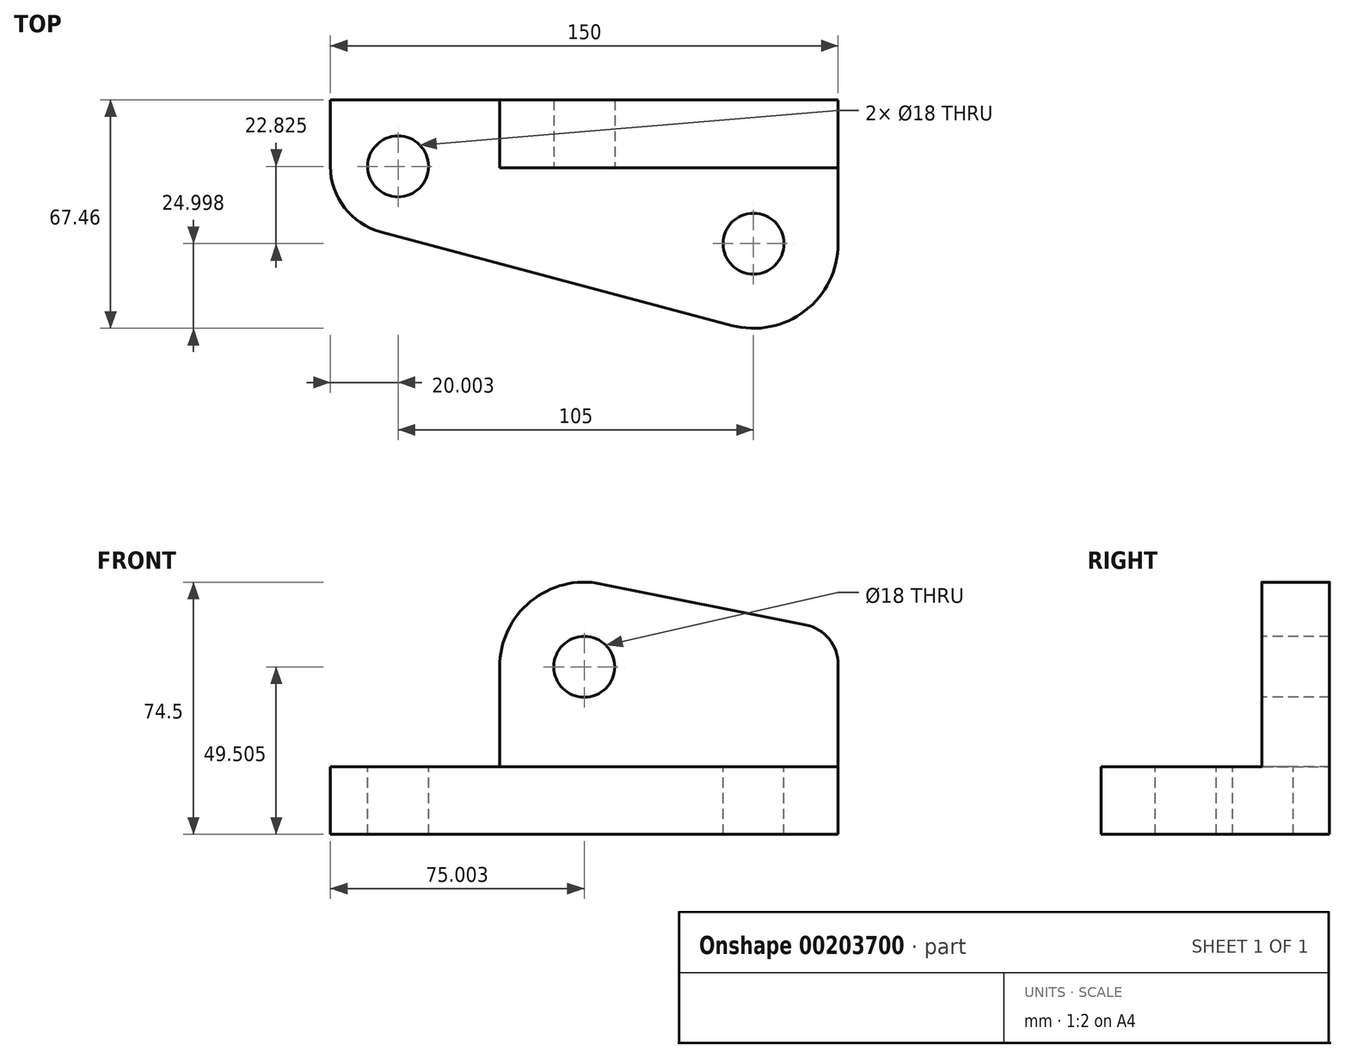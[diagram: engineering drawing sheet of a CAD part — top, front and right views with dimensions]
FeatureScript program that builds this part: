
annotation { "Feature Type Name" : "Feature", "Feature Type Description" : "" }
export const myFeature = defineFeature(function(context is Context, id is Id, definition is map)
    precondition{}
    {
        {
            var Q0;
            Q0=qCreatedBy(makeId("Top.planeOp"),FACE);
            var sketch = newSketch(context, id + "F0", { "sketchPlane" : qUnion([Q0])});
            skLineSegment(sketch, "E0", {"start": v(-98.1, 64.12) * mm, "end": v(-98.1, 29.12) * mm});
            skLineSegment(sketch, "E1", {"start": v(-98.1, 64.12) * mm, "end": v(51.9, 64.12) * mm});
            skLineSegment(sketch, "E2", {"start": v(51.9, 64.12) * mm, "end": v(51.9, -10.88) * mm});
            skLineSegment(sketch, "E3", {"start": v(-98.1, 29.12) * mm, "end": v(51.9, -10.88) * mm});
            skSolve(sketch);
        }
        {
            var Q0;
            Q0=makeQuery(id+"F0.imprint","IMPRINT",FACE,{"disambiguationData":[TD([[makeQuery(id+"F0.imprint","IMPRINT",EDGE,{"derivedFrom":sQuery(id+"F0.wireOp",EDGE,"E0")}),1.0]])]});
            extrude(context, id + "F1", {"entities" : qUnion([Q0]), "depth" : 20 * mm});
        }
        {
            var Q0;
            Q0=makeQuery(id+"F1.opExtrude","SWEPT_FACE",FACE,{"disambiguationData":[OSD([sQuery(id+"F0.wireOp",EDGE,"E1")])]});
            var sketch = newSketch(context, id + "F2", { "sketchPlane" : qUnion([Q0])});
            skLineSegment(sketch, "E4", {"start": v(-51.9, 0) * mm, "end": v(48.1, 0) * mm});
            skLineSegment(sketch, "E5", {"start": v(48.1, 0) * mm, "end": v(48.1, 80) * mm});
            skLineSegment(sketch, "E6", {"start": v(-51.9, 0) * mm, "end": v(-51.9, 60) * mm});
            skLineSegment(sketch, "E7", {"start": v(-51.9, 60) * mm, "end": v(48.1, 80) * mm});
            skSolve(sketch);
        }
        {
            var Q0;
            {var subQ0=sQuery(id+"F2.wireOp",EDGE,"E7");Q0=makeQuery(id+"F2.imprint","IMPRINT",FACE,{"disambiguationData":[TD([[makeQuery(id+"F2.imprint","IMPRINT",EDGE,{"derivedFrom":subQ0}),-1.0]])]});}
            extrude(context, id + "F3", {"entities" : qUnion([Q0]), "operationType" : NewBodyOperationType.ADD, "oppositeDirection" : true, "depth" : 20 * mm});
        }
        {
            var Q0;
            Q0=makeQuery(id+"F1.opExtrude","SWEPT_EDGE",EDGE,{"disambiguationData":[OSD([sQuery(id+"F0.wireOp",EDGE,"E0"),sQuery(id+"F0.wireOp",EDGE,"E3")])]});
            fillet(context, id + "F4", {"entities" : qUnion([Q0]), "radius" : 20 * mm, "tangentPropagation" : true, "allowEdgeOverflow" : false});
        }
        {
            var Q0;
            Q0=makeQuery(id+"F1.opExtrude","SWEPT_EDGE",EDGE,{"disambiguationData":[OSD([sQuery(id+"F0.wireOp",EDGE,"E2"),sQuery(id+"F0.wireOp",EDGE,"E3")])]});
            fillet(context, id + "F5", {"entities" : qUnion([Q0]), "radius" : 25 * mm, "tangentPropagation" : true, "allowEdgeOverflow" : false});
        }
        {
            var Q0;
            Q0=makeQuery(id+"F3.opExtrude","SWEPT_EDGE",EDGE,{"disambiguationData":[OSD([sQuery(id+"F2.wireOp",EDGE,"E5"),sQuery(id+"F2.wireOp",EDGE,"E7")])]});
            fillet(context, id + "F6", {"entities" : qUnion([Q0]), "radius" : 25 * mm, "tangentPropagation" : true, "allowEdgeOverflow" : false});
        }
        {
            var Q0;
            Q0=makeQuery(id+"F3.opExtrude","SWEPT_EDGE",EDGE,{"disambiguationData":[OSD([sQuery(id+"F2.wireOp",EDGE,"E6"),sQuery(id+"F2.wireOp",EDGE,"E7")])]});
            fillet(context, id + "F7", {"entities" : qUnion([Q0]), "radius" : 12 * mm, "tangentPropagation" : true, "allowEdgeOverflow" : false});
        }
        {
            var Q0;
            Q0=makeQuery(id+"F1.opExtrude","CAP_FACE",FACE,{"disambiguationData":[OSD([sQuery(id+"F0.wireOp",EDGE,"E0"),sQuery(id+"F0.wireOp",EDGE,"E1"),sQuery(id+"F0.wireOp",EDGE,"E2"),sQuery(id+"F0.wireOp",EDGE,"E3")])],"isStart":false});
            var sketch = newSketch(context, id + "F8", { "sketchPlane" : qUnion([Q0])});
            skPoint(sketch, "E8", {"position": v(-78.1, 44.48) * mm});
            skPoint(sketch, "E9", {"position": v(26.9, 21.66) * mm});
            skSolve(sketch);
        }
        {
            var Q0;
            Q0=makeQuery(id+"F3.opExtrude","CAP_FACE",FACE,{"disambiguationData":[OSD([sQuery(id+"F0.wireOp",EDGE,"E1"),sQuery(id+"F2.wireOp",EDGE,"E5"),sQuery(id+"F2.wireOp",EDGE,"E6"),sQuery(id+"F2.wireOp",EDGE,"E7")])],"isStart":false});
            var sketch = newSketch(context, id + "F9", { "sketchPlane" : qUnion([Q0])});
            skPoint(sketch, "E10", {"position": v(-23.1, 49.5) * mm});
            skSolve(sketch);
        }
        {
            var Q0;
            Q0=sQuery(id+"F9.wireOp",VERTEX,"E10");
            var Q1;
            Q1=makeQuery(id+"F1.opExtrude","SWEPT_BODY",BODY,{"disambiguationData":[OSD([sQuery(id+"F0.wireOp",EDGE,"E0"),sQuery(id+"F0.wireOp",EDGE,"E1"),sQuery(id+"F0.wireOp",EDGE,"E2"),sQuery(id+"F0.wireOp",EDGE,"E3")])]});
            hole(context, id + "F10", {"style" : HoleStyle.SIMPLE, "endStyle" : HoleEndStyle.THROUGH, "holeDiameter" : 18 * mm, "locations" : qUnion([Q0]), "scope" : qUnion([Q1]), "isTappedThrough" : true});
        }
        {
            var Q0;
            Q0=sQuery(id+"F8.wireOp",VERTEX,"E8");
            var Q1;
            Q1=makeQuery(id+"F1.opExtrude","SWEPT_BODY",BODY,{"disambiguationData":[OSD([sQuery(id+"F0.wireOp",EDGE,"E0"),sQuery(id+"F0.wireOp",EDGE,"E1"),sQuery(id+"F0.wireOp",EDGE,"E2"),sQuery(id+"F0.wireOp",EDGE,"E3")])]});
            hole(context, id + "F11", {"style" : HoleStyle.SIMPLE, "endStyle" : HoleEndStyle.THROUGH, "holeDiameter" : 18 * mm, "locations" : qUnion([Q0]), "scope" : qUnion([Q1]), "isTappedThrough" : true});
        }
        {
            var Q0;
            Q0=makeQuery(id+"F1.opExtrude","CAP_FACE",FACE,{"disambiguationData":[OSD([sQuery(id+"F0.wireOp",EDGE,"E0"),sQuery(id+"F0.wireOp",EDGE,"E1"),sQuery(id+"F0.wireOp",EDGE,"E2"),sQuery(id+"F0.wireOp",EDGE,"E3")])],"isStart":false});
            var sketch = newSketch(context, id + "F12", { "sketchPlane" : qUnion([Q0])});
            skPoint(sketch, "E11", {"position": v(26.9, 21.66) * mm});
            skSolve(sketch);
        }
        {
            var Q0;
            Q0=sQuery(id+"F12.wireOp",VERTEX,"E11");
            var Q1;
            Q1=makeQuery(id+"F1.opExtrude","SWEPT_BODY",BODY,{"disambiguationData":[OSD([sQuery(id+"F0.wireOp",EDGE,"E0"),sQuery(id+"F0.wireOp",EDGE,"E1"),sQuery(id+"F0.wireOp",EDGE,"E2"),sQuery(id+"F0.wireOp",EDGE,"E3")])]});
            hole(context, id + "F13", {"style" : HoleStyle.SIMPLE, "endStyle" : HoleEndStyle.THROUGH, "holeDiameter" : 18 * mm, "locations" : qUnion([Q0]), "scope" : qUnion([Q1]), "isTappedThrough" : true});
        }
    });
